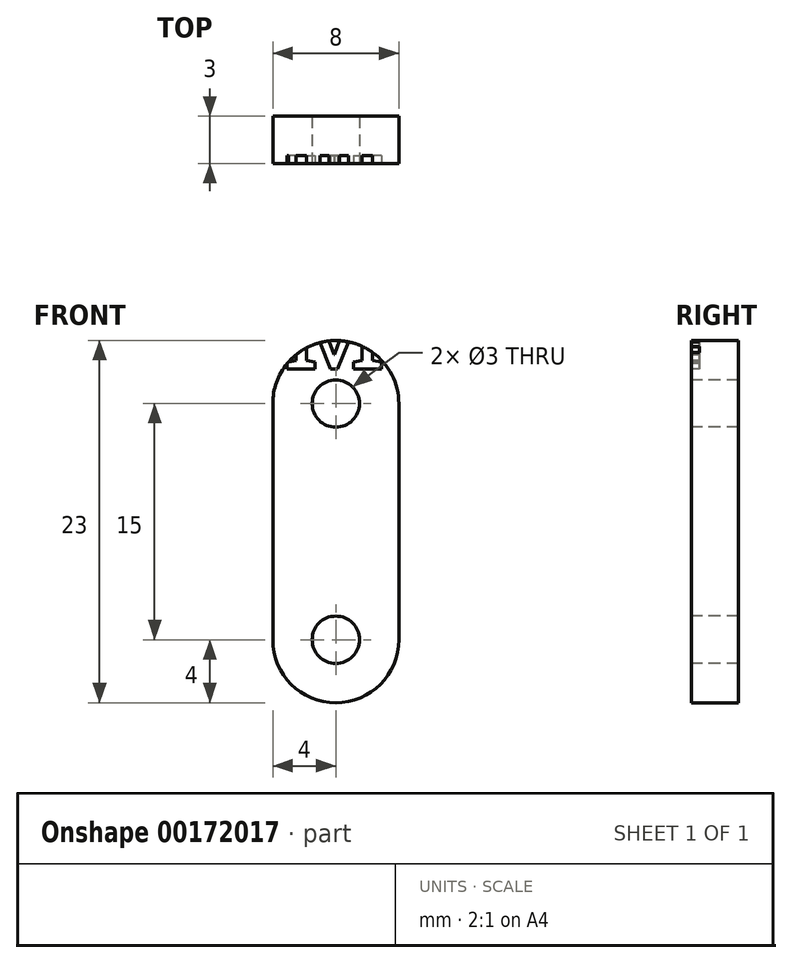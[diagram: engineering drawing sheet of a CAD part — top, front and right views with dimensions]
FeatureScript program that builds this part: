
annotation { "Feature Type Name" : "Feature", "Feature Type Description" : "" }
export const myFeature = defineFeature(function(context is Context, id is Id, definition is map)
    precondition{}
    {
        {
            assignVariable(context, id + "F0", {"name" : "Thickness", "anyValue" : 3});
        }
        {
            var Q0;
            Q0=qCreatedBy(makeId("Front.planeOp"),FACE);
            var sketch = newSketch(context, id + "F1", { "sketchPlane" : qUnion([Q0])});
            skCircle(sketch, "E0", {"center": v(0, 15) * mm, "radius": 1.5 * mm});
            skCircle(sketch, "E1", {"center": v(0, 0) * mm, "radius": 1.5 * mm});
            skArc(sketch, "E2", {"start": v(4, 15) * mm, "mid": v(0, 19) * mm, "end": v(-4, 15) * mm});
            skArc(sketch, "E3", {"start": v(-4, 0) * mm, "mid": v(0, -4) * mm, "end": v(4, 0) * mm});
            skLineSegment(sketch, "E4", {"start": v(-4, 0) * mm, "end": v(-4, 15) * mm});
            skLineSegment(sketch, "E5", {"start": v(4, 15) * mm, "end": v(4, 0) * mm});
            skSolve(sketch);
        }
        {
            var Q0;
            Q0=makeQuery(id+"F1.imprint","IMPRINT",FACE,{"disambiguationData":[TD([[makeQuery(id+"F1.imprint","IMPRINT",EDGE,{"derivedFrom":sQuery(id+"F1.wireOp",EDGE,"E0")}),-1.0]])]});
            extrude(context, id + "F2", {"entities" : qUnion([Q0]), "oppositeDirection" : true, "depth" : (getVariable(context, 'Thickness')) * mm});
        }
        {
            var Q0;
            Q0=qCreatedBy(makeId("Front.planeOp"),FACE);
            var sketch = newSketch(context, id + "F3", { "sketchPlane" : qUnion([Q0])});
            skText(sketch, "E6", { "text": "M", "fontName": "RobotoSlab-Regular.ttf"});
            skLineSegment(sketch, "E7", {"start": v(4, 7.5) * mm, "end": v(2, 7.5) * mm, "construction": true});
            const initialGuessF3  = {"E6": [-0.00333, 0.0172, 1, 0, 0.005]};
            skSetInitialGuess(sketch, initialGuessF3);
            skSolve(sketch);
        }
        {
            assignVariable(context, id + "F4", {"name" : "DepthText", "anyValue" : .5});
        }
        {
            var Q0;
            Q0=qSketchRegion(id+"F3",true);
            extrude(context, id + "F5", {"entities" : qUnion([Q0]), "operationType" : NewBodyOperationType.REMOVE, "oppositeDirection" : true, "depth" : (getVariable(context, 'DepthText')) * mm});
        }
    });
